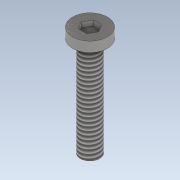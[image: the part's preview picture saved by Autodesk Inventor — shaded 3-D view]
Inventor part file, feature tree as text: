
AUTODESK INVENTOR PART (.ipt)
format: ipt  version: 2022 (Build 260153000, 153)  size: 124,928 bytes
history: native  units: mm
features: extrude x3, sketch x3, thread x1
ambient origin geometry x8: Origin, YZ Plane, XZ Plane, XY Plane, X Axis, Y Axis, Z Axis, Center Point
bodies: Solid1 (feature_tree)
feature tree (7):
  extrude  "Extrusion1"  Depth=20.0mm TaperAngle=0.0deg
  extrude  "Extrusion2"  Depth=2.0mm TaperAngle=0.0deg
  thread  "Thread1"  [1 undecoded]
  extrude  "Extrusion3"  Depth=1.0mm TaperAngle=0.0deg
  sketch  "Sketch1"  dims[d0=3.9mm d1=20.0mm d2=0.0mm]
  sketch  "Sketch2"  dims[d3=7.0mm d4=2.0mm d5=0.0mm d6=20.0mm d7=0.0mm]
  sketch  "Sketch3"  dims[d8=3.0mm d9=1.0mm d10=0.0mm]
note: 1 required parameter value undecoded (feature->parameter linkage not recoverable at this tier; creation-order binding heuristic only, values carry confidence <= 0.55)
